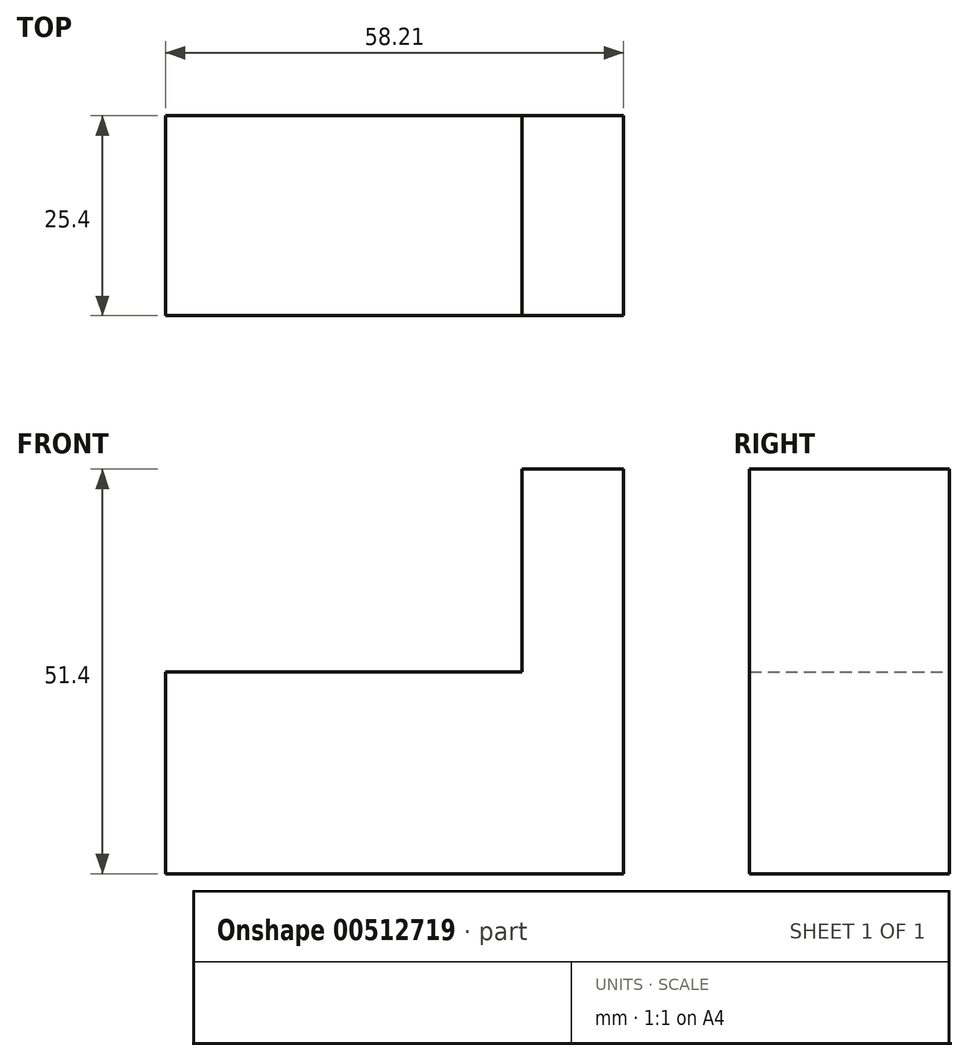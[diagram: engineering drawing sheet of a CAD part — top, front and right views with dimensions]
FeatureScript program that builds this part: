
annotation { "Feature Type Name" : "Feature", "Feature Type Description" : "" }
export const myFeature = defineFeature(function(context is Context, id is Id, definition is map)
    precondition{}
    {
        {
            var Q0;
            Q0=qCreatedBy(makeId("Front.planeOp"),FACE);
            var sketch = newSketch(context, id + "F0", { "sketchPlane" : qUnion([Q0])});
            skLineSegment(sketch, "E0.bottom", {"start": v(-37.62, 77.98) * mm, "end": v(-3.32, 77.98) * mm});
            skLineSegment(sketch, "E0.top", {"start": v(-37.62, 25.74) * mm, "end": v(-3.32, 25.74) * mm});
            skLineSegment(sketch, "E0.left", {"start": v(-37.62, 77.98) * mm, "end": v(-37.62, 25.74) * mm});
            skLineSegment(sketch, "E0.right", {"start": v(-3.32, 77.98) * mm, "end": v(-3.32, 25.74) * mm});
            skLineSegment(sketch, "E1.bottom", {"start": v(54.89, -25.66) * mm, "end": v(-3.32, -25.66) * mm});
            skLineSegment(sketch, "E1.top", {"start": v(54.89, 25.74) * mm, "end": v(-3.32, 25.74) * mm});
            skLineSegment(sketch, "E1.left", {"start": v(54.89, -25.66) * mm, "end": v(54.89, 25.74) * mm});
            skLineSegment(sketch, "E1.right", {"start": v(-3.32, -25.66) * mm, "end": v(-3.32, 25.74) * mm});
            skLineSegment(sketch, "E2.bottom", {"start": v(42, 0) * mm, "end": v(-3.32, 0) * mm});
            skLineSegment(sketch, "E2.top", {"start": v(42, 25.74) * mm, "end": v(-3.32, 25.74) * mm});
            skLineSegment(sketch, "E2.left", {"start": v(42, 0) * mm, "end": v(42, 25.74) * mm});
            skLineSegment(sketch, "E2.right", {"start": v(-3.32, 0) * mm, "end": v(-3.32, 25.74) * mm});
            skSolve(sketch);
        }
        {
            var Q0;
            Q0=makeQuery(id+"F0.imprint","IMPRINT",FACE,{"disambiguationData":[TD([[makeQuery(id+"F0.imprint","IMPRINT",EDGE,{"derivedFrom":sQuery(id+"F0.wireOp",EDGE,"E1.bottom")}),-1.0]])]});
            extrude(context, id + "F1", {"entities" : qUnion([Q0]), "depth" : 25.4 * mm});
        }
    });
